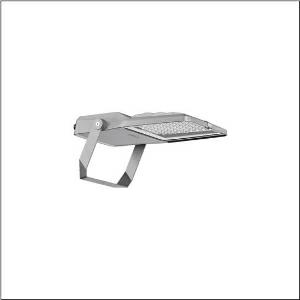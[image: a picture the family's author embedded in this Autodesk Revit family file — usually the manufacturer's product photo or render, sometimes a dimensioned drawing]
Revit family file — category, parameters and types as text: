
# Revit family: floodlight_fl_21_iq_mini___pl61_5xa7772b3c1a_b78d
name_source: partatom
category: Lighting Fixtures
units: mm (PartAtom-declared; Revit-internal decimal feet)

## family parameters
Cut with Voids When Loaded = No
Host = Face
Light Source = No
Part Type = Normal
Room Calculation Point = No
Round Connector Dimension = Use Diameter
Shared = No

## types (1)
- --- (1 x LED, 5270 lm, 45.5 W, 3000K)
    Apparent Load = 46 VA
    CIE Flux Codes = 33 65 98 100 100
    Color Rendering = 80
    Color Temperature = 3000K
    Default Elevation = 1800 mm
    Description = Floodlight FL 21 iQ mini, floodlight, primary light control with lens, of PMMA, primary optical cover: protective disc, of toughened safety glass, transparent, light distribution: PL61, light emission: direct distribution, installation type: surface-mounted, LED, High Power LED, rated luminous flux: 5.270lm, luminous efficacy: 116lm/W, light colour: 830, colour temperature: 3000K, control gear: iQ Street-Remote/DALI, control: Street-Remote, Auto-Match, Temp-Guard, Night-Set, Smart-Wire, Desk-Remote (wireless, voltage-free reading and setting of iQ features in the workshop via application-optimized NFC function/RFID function), optimised constant luminous flux control (CLO 2.0), with terminal, 6-pole, mains connection: 220..240V, AC, 50/60Hz, start of lifetime: 46W, end of service life: 48W, reduction: 21W, luminaire housing, of diecast aluminium, powder-coated, Siteco® metallic grey (DB 702S), corrosivity category C5 mid according to DIN EN ISO 12944, suitable for swimming pools, chlorine-resistant, sealing non-destructively replaceable, mounting bracket, of steel, galvanised, powder-coated, Siteco® metallic grey (DB 702S), protection rating (complete): IP66, insulation class (complete): insulation class II (safety insulation), certification: CE, ENEC, VDE, protection symbol: D, impact resistance: IK08, permissible operating ambient temperature: -40..+40°C, permissible operating ambient temperature for outdoor applications: -40..+50°C, standard: DIN EN 12944, LABS conformity tested according to VDMA 24364:2018-05, packaging unit: 1 piece

Light Distribution: PL61
    Height = 70 mm
    Lamp = 1 x LED
    Lamp Light Flux = 5270 lm
    Lamp Power = 45.5 W
    Lamp count = 1
    Length = 485 mm
    Luminous efficacy = 116 lm/W
    Manufacturer = Siteco
    ModVariant = No
    Model = 5XA7772B3C1A
    Number of Poles = 1
    OnlyDefault = Yes
    Power Factor = 1
    Product Name = Floodlight FL 21 iQ mini | PL61
    Product group = floodlight | pylon annexe
    ProductGroupID = 6200
    Protection Class = Protection class II
    Protection Degree = IP 66
    RLX_Detail_Level = 1
    RLX_Emergency_Light_Flux = 0 lm
    RLX_Emergency_Type = 0
    RLX_Emergency_Type_DB = No
    RlxData = <blob elided: 96245 chars, md5=02156370>
    Socket = socket
    Standby Power = 0 W
    System Light Flux = 5270 lm
    System Power = 46 W
    Type Comments = factory setting: luminous flux: 100 % | dim-lin: 254 | 463 mA
    Type Image = l_1006845.jpg
    URL = http://relux.com
    VarID = @adj_173548
    Voltage = 0 V
    Weight = 0.00 kg
    Width = 337 mm

## geometry (parser evidence)
native form markers: Blend x4, Sweep x11
no freeform markers — native parametric forms only
